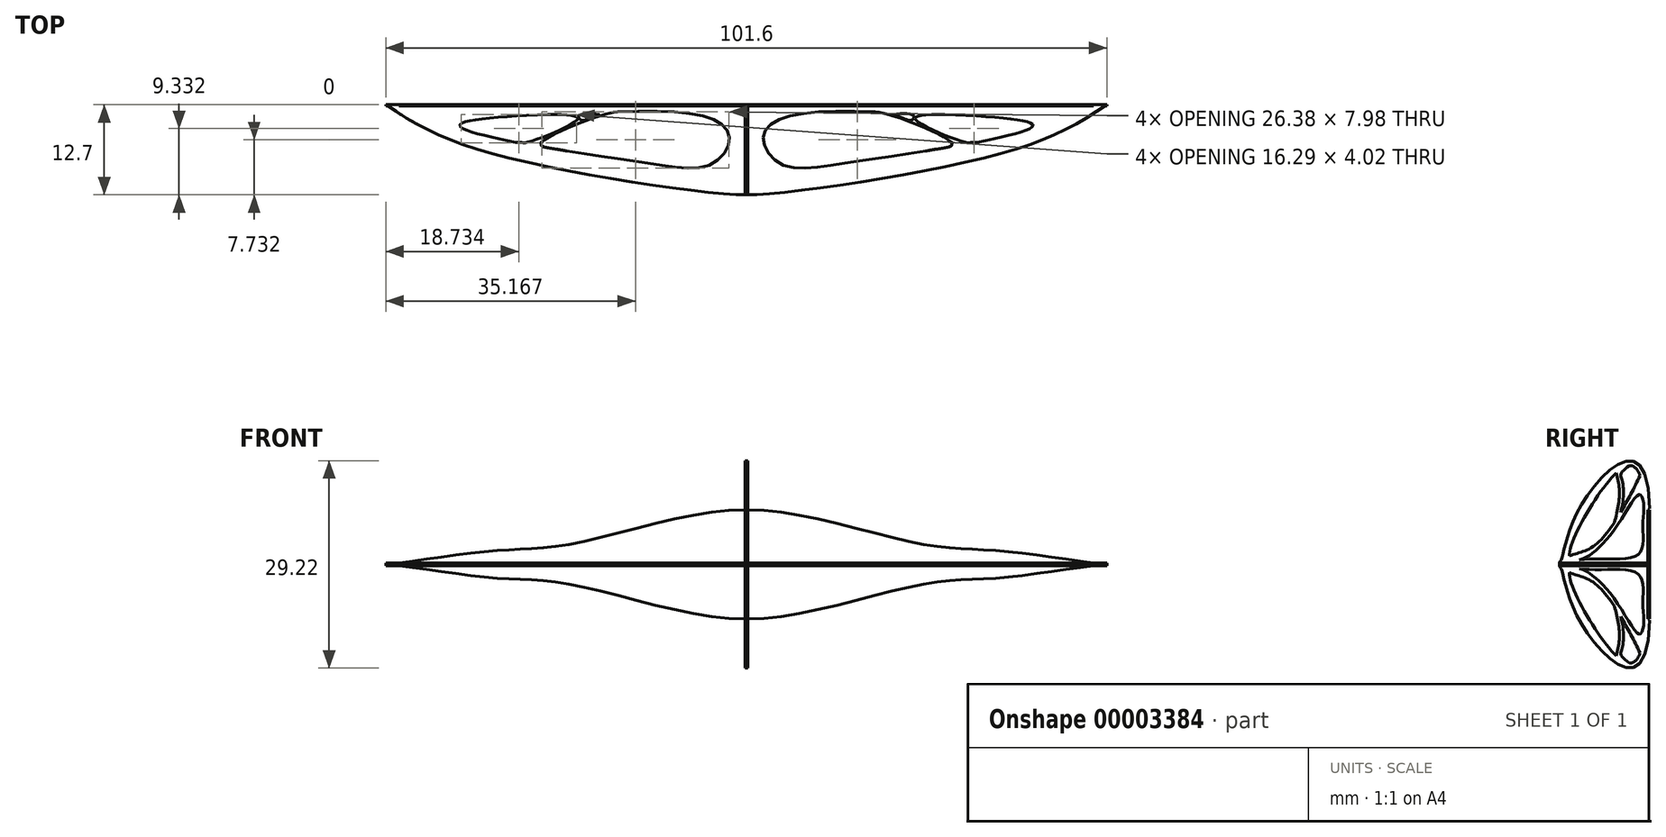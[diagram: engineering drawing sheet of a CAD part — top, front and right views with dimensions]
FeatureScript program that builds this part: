
annotation { "Feature Type Name" : "Feature", "Feature Type Description" : "" }
export const myFeature = defineFeature(function(context is Context, id is Id, definition is map)
    precondition{}
    {
        {
            var Q0;
            Q0=qCreatedBy(makeId("Top.planeOp"),FACE);
            var sketch = newSketch(context, id + "F0", { "sketchPlane" : qUnion([Q0])});
            skLineSegment(sketch, "E0", {"start": v(-50.8, 0) * mm, "end": v(0, 0) * mm});
            skFitSpline(sketch, "E1", {"points": [v(-50.8, 0) * mm, v(-34.32, -7.28) * mm, v(0, -12.7) * mm], "startDerivative": vector(33.72, -23.22) * mm, "endDerivative": vector(28.54, 0.13) * mm});
            skLineSegment(sketch, "E2", {"start": v(0, 0) * mm, "end": v(0, -12.7) * mm});
            skFitSpline(sketch, "E3", {"points": [v(-4.93, -1.97) * mm, v(-2.37, -4.74) * mm, v(-4.94, -8.4) * mm, v(-13.42, -8.32) * mm, v(-29.98, -5.77) * mm, v(-40.37, -2.89) * mm, v(-22.94, -1.15) * mm, v(-4.93, -1.97) * mm]});
            skFitSpline(sketch, "E4", {"points": [v(-32.52, -5.3) * mm, v(-30.8, -5.3) * mm, v(-23.82, -2.1) * mm, v(-27.98, -1.36) * mm], "startDerivative": vector(14.9, 0) * mm, "endDerivative": vector(-23.52, 0.36) * mm});
            skFitSpline(sketch, "E5", {"points": [v(-18.18, -0.98) * mm, v(-22.9, -2.36) * mm, v(-29, -5.66) * mm, v(-25.3, -6.56) * mm], "startDerivative": vector(-11.87, -1.95) * mm, "endDerivative": vector(11.84, -3.74) * mm});
            skFitSpline(sketch, "E6", {"points": [v(-23.21, -2.2) * mm, v(-23.6, -1.53) * mm, v(-20.69, -1.42) * mm, v(-21.83, -1.8) * mm, v(-23.21, -2.2) * mm]});
            skLineSegment(sketch, "E7", {"start": v(-0.2, 0) * mm, "end": v(-0.2, -7.32) * mm});
            skLineSegment(sketch, "E8", {"start": v(-0.2, -7.32) * mm, "end": v(0, -7.32) * mm});
            skSolve(sketch);
        }
        {
            var Q0;
            {var subQ10=sQuery(id+"F0.wireOp",EDGE,"E1");Q0=makeQuery(id+"F0.imprint","IMPRINT",FACE,{"disambiguationData":[TD([[makeQuery(id+"F0.imprint","IMPRINT",EDGE,{"derivedFrom":subQ10}),1.0]])]});}
            var Q1;
            {var subQ1=sQuery(id+"F0.wireOp",EDGE,"E4");Q1=makeQuery(id+"F0.imprint","IMPRINT",FACE,{"disambiguationData":[TD([[makeQuery(id+"F0.imprint","IMPRINT",EDGE,{"derivedFrom":subQ1}),-1.0]])]});}
            extrude(context, id + "F1", {"entities" : qUnion([Q0, Q1]), "depth" : 0.2 * mm});
        }
        {
            var Q0;
            Q0=qCreatedBy(makeId("Front.planeOp"),FACE);
            var sketch = newSketch(context, id + "F2", { "sketchPlane" : qUnion([Q0])});
            skFitSpline(sketch, "E9", {"points": [v(0, 7.68) * mm, v(-24.54, 2.88) * mm, v(-35.92, 1.89) * mm, v(-50.8, 0) * mm], "startDerivative": vector(-51.84, 1.83) * mm, "endDerivative": vector(-38.42, -3.43) * mm});
            skLineSegment(sketch, "E10", {"start": v(0, 0) * mm, "end": v(0, 7.68) * mm});
            skLineSegment(sketch, "E11", {"start": v(-50.8, 0) * mm, "end": v(0, 0) * mm});
            skLineSegment(sketch, "E12", {"start": v(-0.2, 0) * mm, "end": v(-0.2, 7.69) * mm});
            skSolve(sketch);
        }
        {
            var Q0;
            {var subQ0=sQuery(id+"F2.wireOp",EDGE,"E12");Q0=makeQuery(id+"F2.imprint","IMPRINT",FACE,{"disambiguationData":[TD([[makeQuery(id+"F2.imprint","IMPRINT",EDGE,{"derivedFrom":subQ0}),1.0]])]});}
            extrude(context, id + "F3", {"entities" : qUnion([Q0]), "operationType" : NewBodyOperationType.ADD, "depth" : 0.2 * mm});
        }
        {
            var Q0;
            Q0=qCreatedBy(makeId("Right.planeOp"),FACE);
            var sketch = newSketch(context, id + "F4", { "sketchPlane" : qUnion([Q0])});
            skLineSegment(sketch, "E13", {"start": v(0, 0) * mm, "end": v(-12.7, 0) * mm});
            skFitSpline(sketch, "E14", {"points": [v(-12.7, 0) * mm, v(-12.49, 0.51) * mm, v(-8.69, 9.8) * mm, v(0, 7.62) * mm], "startDerivative": vector(-0.45, 11.17) * mm, "endDerivative": vector(0, -78.16) * mm});
            skLineSegment(sketch, "E15", {"start": v(0, 7.62) * mm, "end": v(0, 0) * mm});
            skFitSpline(sketch, "E16", {"points": [v(-0.91, 4.96) * mm, v(-0.82, 10.12) * mm, v(-2.16, 13.75) * mm, v(-5.45, 12.07) * mm, v(-11.25, 1.05) * mm, v(-8.62, 0.73) * mm, v(-1.61, 1.35) * mm, v(-0.91, 4.96) * mm]});
            skFitSpline(sketch, "E17", {"points": [v(-1.3, 12.5) * mm, v(-3.44, 8.4) * mm, v(-7.78, 2.62) * mm, v(-11.27, 1.19) * mm], "startDerivative": vector(-5.72, -11.95) * mm, "endDerivative": vector(-11.41, -4.3) * mm});
            skFitSpline(sketch, "E18", {"points": [v(-4.94, 5.9) * mm, v(-4.22, 9.76) * mm, v(-4.65, 12.9) * mm], "startDerivative": vector(2.14, 7.4) * mm, "endDerivative": vector(-1.47, 6.4) * mm});
            skFitSpline(sketch, "E19", {"points": [v(-0.78, 8.65) * mm, v(-1.38, 9.84) * mm, v(-4.65, 5.29) * mm, v(-8.4, 1.3) * mm, v(-9.86, 0.62) * mm], "startDerivative": vector(-2.48, 11.14) * mm, "endDerivative": vector(-7.74, -2.2) * mm});
            skFitSpline(sketch, "E20", {"points": [v(-4.03, 7.37) * mm, v(-3.64, 10.04) * mm, v(-3.89, 11.93) * mm, v(-4.03, 12.68) * mm, v(-2.84, 13.92) * mm], "startDerivative": vector(1.93, 8.52) * mm, "endDerivative": vector(6.45, 5.1) * mm});
            skSolve(sketch);
        }
        {
            var Q0;
            Q0=makeQuery(id+"F4.imprint","IMPRINT",FACE,{"disambiguationData":[TD([[makeQuery(id+"F4.imprint","IMPRINT",EDGE,{"derivedFrom":sQuery(id+"F4.wireOp",EDGE,"E13")}),-1.0]])]});
            var Q1;
            {var subQ6=sQuery(id+"F4.wireOp",EDGE,"E19");Q1=makeQuery(id+"F4.imprint","IMPRINT",FACE,{"disambiguationData":[TD([[makeQuery(id+"F4.imprint","IMPRINT",EDGE,{"derivedFrom":subQ6}),-1.0]])]});}
            var Q2;
            {var subQ1=sQuery(id+"F4.wireOp",EDGE,"E18");Q2=makeQuery(id+"F4.imprint","IMPRINT",FACE,{"disambiguationData":[TD([[makeQuery(id+"F4.imprint","IMPRINT",EDGE,{"derivedFrom":subQ1}),-1.0]])]});}
            extrude(context, id + "F5", {"entities" : qUnion([Q0, Q1, Q2]), "depth" : 0.2 * mm});
        }
        {
            var Q0;
            Q0=makeQuery(id+"F1.opExtrude","SWEPT_BODY",BODY,{"disambiguationData":[OSD([sQuery(id+"F0.wireOp",EDGE,"E0"),sQuery(id+"F0.wireOp",EDGE,"E1"),sQuery(id+"F0.wireOp",EDGE,"E2"),sQuery(id+"F0.wireOp",EDGE,"E3"),sQuery(id+"F0.wireOp",EDGE,"E4"),sQuery(id+"F0.wireOp",EDGE,"E5"),sQuery(id+"F0.wireOp",EDGE,"E6"),sQuery(id+"F0.wireOp",EDGE,"E7"),sQuery(id+"F0.wireOp",EDGE,"E8")])]});
            var Q1;
            Q1=makeQuery(id+"F5.opExtrude","SWEPT_BODY",BODY,{"disambiguationData":[OSD([sQuery(id+"F4.wireOp",EDGE,"E13"),sQuery(id+"F4.wireOp",EDGE,"E14"),sQuery(id+"F4.wireOp",EDGE,"E15"),sQuery(id+"F4.wireOp",EDGE,"E16"),sQuery(id+"F4.wireOp",EDGE,"E17"),sQuery(id+"F4.wireOp",EDGE,"E18"),sQuery(id+"F4.wireOp",EDGE,"E19"),sQuery(id+"F4.wireOp",EDGE,"E20")])]});
            var Q2;
            Q2=qCreatedBy(makeId("Right.planeOp"),FACE);
            mirror(context, id + "F6", {"entities" : qUnion([Q0, Q1]), "mirrorPlane" : qUnion([Q2])});
        }
        {
            var Q0;
            Q0=makeQuery(id+"F1.opExtrude","SWEPT_BODY",BODY,{"disambiguationData":[OSD([sQuery(id+"F0.wireOp",EDGE,"E0"),sQuery(id+"F0.wireOp",EDGE,"E1"),sQuery(id+"F0.wireOp",EDGE,"E2"),sQuery(id+"F0.wireOp",EDGE,"E3"),sQuery(id+"F0.wireOp",EDGE,"E4"),sQuery(id+"F0.wireOp",EDGE,"E5"),sQuery(id+"F0.wireOp",EDGE,"E6"),sQuery(id+"F0.wireOp",EDGE,"E7"),sQuery(id+"F0.wireOp",EDGE,"E8")])]});
            var Q1;
            Q1=makeQuery(id+"F6.opPattern","COPY",BODY,{"derivedFrom":makeQuery(id+"F1.opExtrude","SWEPT_BODY",BODY,{"disambiguationData":[OSD([sQuery(id+"F0.wireOp",EDGE,"E0"),sQuery(id+"F0.wireOp",EDGE,"E1"),sQuery(id+"F0.wireOp",EDGE,"E2"),sQuery(id+"F0.wireOp",EDGE,"E3"),sQuery(id+"F0.wireOp",EDGE,"E4"),sQuery(id+"F0.wireOp",EDGE,"E5"),sQuery(id+"F0.wireOp",EDGE,"E6"),sQuery(id+"F0.wireOp",EDGE,"E7"),sQuery(id+"F0.wireOp",EDGE,"E8")])]}),"instanceName":"1"});
            var Q2;
            Q2=makeQuery(id+"F5.opExtrude","SWEPT_BODY",BODY,{"disambiguationData":[OSD([sQuery(id+"F4.wireOp",EDGE,"E13"),sQuery(id+"F4.wireOp",EDGE,"E14"),sQuery(id+"F4.wireOp",EDGE,"E15"),sQuery(id+"F4.wireOp",EDGE,"E16"),sQuery(id+"F4.wireOp",EDGE,"E17"),sQuery(id+"F4.wireOp",EDGE,"E18"),sQuery(id+"F4.wireOp",EDGE,"E19"),sQuery(id+"F4.wireOp",EDGE,"E20")])]});
            var Q3;
            Q3=makeQuery(id+"F6.opPattern","COPY",BODY,{"derivedFrom":makeQuery(id+"F5.opExtrude","SWEPT_BODY",BODY,{"disambiguationData":[OSD([sQuery(id+"F4.wireOp",EDGE,"E13"),sQuery(id+"F4.wireOp",EDGE,"E14"),sQuery(id+"F4.wireOp",EDGE,"E15"),sQuery(id+"F4.wireOp",EDGE,"E16"),sQuery(id+"F4.wireOp",EDGE,"E17"),sQuery(id+"F4.wireOp",EDGE,"E18"),sQuery(id+"F4.wireOp",EDGE,"E19"),sQuery(id+"F4.wireOp",EDGE,"E20")])]}),"instanceName":"1"});
            var Q4;
            Q4=qCreatedBy(makeId("Top.planeOp"),FACE);
            mirror(context, id + "F7", {"entities" : qUnion([Q0, Q1, Q2, Q3]), "mirrorPlane" : qUnion([Q4])});
        }
    });
